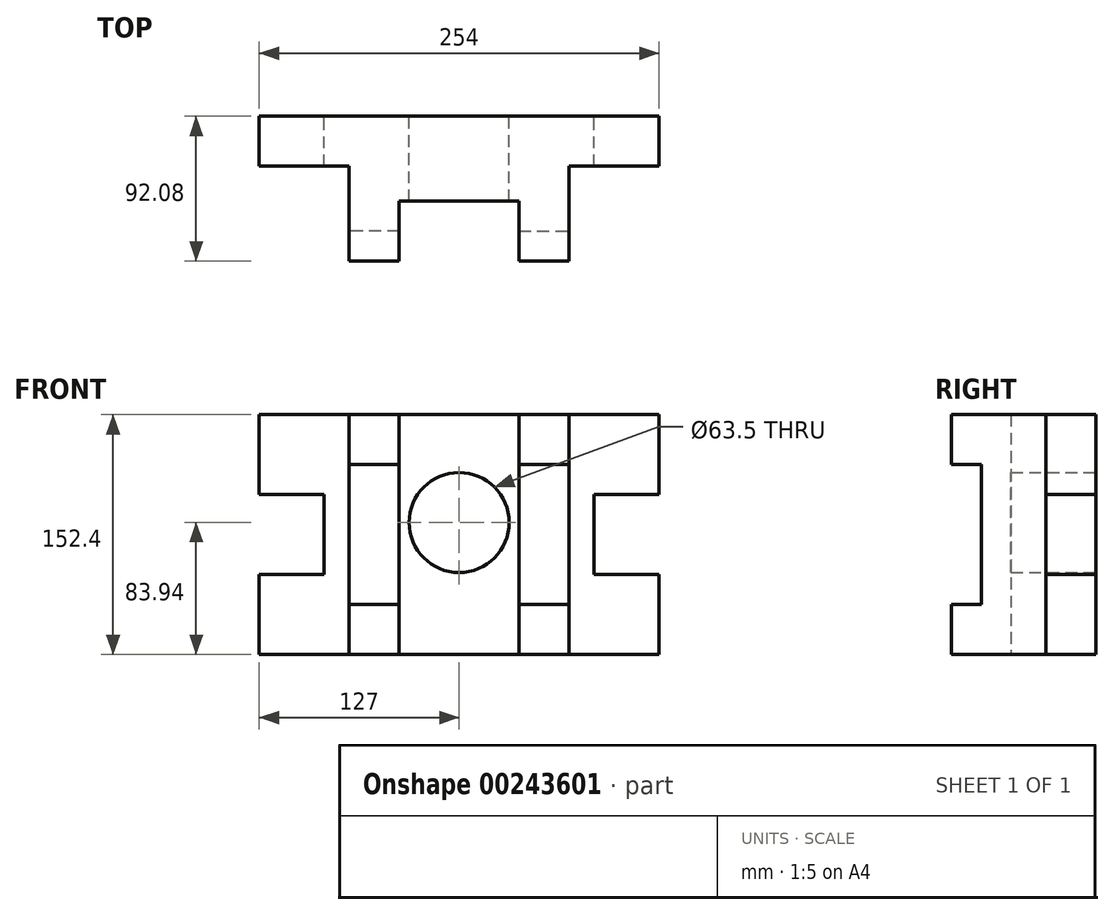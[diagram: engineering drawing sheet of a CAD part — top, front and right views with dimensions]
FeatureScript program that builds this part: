
annotation { "Feature Type Name" : "Feature", "Feature Type Description" : "" }
export const myFeature = defineFeature(function(context is Context, id is Id, definition is map)
    precondition{}
    {
        {
            var Q0;
            Q0=qCreatedBy(makeId("Front.planeOp"),FACE);
            var sketch = newSketch(context, id + "F0", { "sketchPlane" : qUnion([Q0])});
            skLineSegment(sketch, "E0", {"start": v(0, 68.46) * mm, "end": v(0, -79.2) * mm});
            skLineSegment(sketch, "E1.bottom", {"start": v(0, 68.46) * mm, "end": v(38.1, 68.46) * mm});
            skLineSegment(sketch, "E1.top", {"start": v(0, -83.94) * mm, "end": v(38.1, -83.94) * mm});
            skLineSegment(sketch, "E1.left", {"start": v(0, 68.46) * mm, "end": v(0, -83.94) * mm});
            skLineSegment(sketch, "E1.right", {"start": v(38.1, 68.46) * mm, "end": v(38.1, -83.94) * mm});
            skLineSegment(sketch, "E2.bottom", {"start": v(38.1, 68.46) * mm, "end": v(69.85, 68.46) * mm});
            skLineSegment(sketch, "E2.top", {"start": v(38.1, 36.71) * mm, "end": v(69.85, 36.71) * mm});
            skLineSegment(sketch, "E2.left", {"start": v(38.1, 68.46) * mm, "end": v(38.1, 36.71) * mm});
            skLineSegment(sketch, "E2.right", {"start": v(69.85, 68.46) * mm, "end": v(69.85, 36.71) * mm});
            skLineSegment(sketch, "E3.bottom", {"start": v(38.1, -83.94) * mm, "end": v(69.85, -83.94) * mm});
            skLineSegment(sketch, "E3.top", {"start": v(38.1, -52.19) * mm, "end": v(69.85, -52.19) * mm});
            skLineSegment(sketch, "E3.left", {"start": v(38.1, -83.94) * mm, "end": v(38.1, -52.19) * mm});
            skLineSegment(sketch, "E3.right", {"start": v(69.85, -83.94) * mm, "end": v(69.85, -52.19) * mm});
            skLineSegment(sketch, "E4.left", {"start": v(38.1, 36.71) * mm, "end": v(38.1, -52.19) * mm});
            skLineSegment(sketch, "E4.right", {"start": v(69.85, 36.71) * mm, "end": v(69.85, -52.19) * mm});
            skLineSegment(sketch, "E5.bottom", {"start": v(69.85, 68.46) * mm, "end": v(127, 68.46) * mm});
            skLineSegment(sketch, "E5.top", {"start": v(69.85, -83.94) * mm, "end": v(127, -83.94) * mm});
            skLineSegment(sketch, "E5.left", {"start": v(69.85, 68.46) * mm, "end": v(69.85, -83.94) * mm});
            skLineSegment(sketch, "E5.right", {"start": v(127, 68.46) * mm, "end": v(127, 17.66) * mm});
            skLineSegment(sketch, "E6.bottom", {"start": v(127, -83.94) * mm, "end": v(111.13, -83.94) * mm});
            skLineSegment(sketch, "E6.top", {"start": v(127, -33.14) * mm, "end": v(85.72, -33.14) * mm});
            skLineSegment(sketch, "E6.left", {"start": v(127, -83.94) * mm, "end": v(127, -33.14) * mm});
            skLineSegment(sketch, "E7.bottom", {"start": v(85.72, -33.14) * mm, "end": v(127, -33.14) * mm});
            skLineSegment(sketch, "E7.top", {"start": v(85.72, 17.66) * mm, "end": v(127, 17.66) * mm});
            skLineSegment(sketch, "E7.left", {"start": v(85.72, -33.14) * mm, "end": v(85.72, 17.66) * mm});
            skLineSegment(sketch, "E8.MirrorCS", {"start": v(0, 68.46) * mm, "end": v(-38.1, 68.46) * mm});
            skLineSegment(sketch, "E9.MirrorCS", {"start": v(-38.1, 68.46) * mm, "end": v(-38.1, 36.71) * mm});
            skLineSegment(sketch, "E10.MirrorCS", {"start": v(-38.1, 68.46) * mm, "end": v(-38.1, -83.94) * mm});
            skLineSegment(sketch, "E11.MirrorCS", {"start": v(-38.1, 36.71) * mm, "end": v(-69.85, 36.71) * mm});
            skLineSegment(sketch, "E12.MirrorCS", {"start": v(-38.1, -52.19) * mm, "end": v(-69.85, -52.19) * mm});
            skLineSegment(sketch, "E13.MirrorCS", {"start": v(0, -83.94) * mm, "end": v(-38.1, -83.94) * mm});
            skLineSegment(sketch, "E14.MirrorCS", {"start": v(-38.1, -83.94) * mm, "end": v(-69.85, -83.94) * mm});
            skLineSegment(sketch, "E15.MirrorCS", {"start": v(-69.85, -83.94) * mm, "end": v(-127, -83.94) * mm});
            skLineSegment(sketch, "E16.MirrorCS", {"start": v(-127, -33.14) * mm, "end": v(-85.72, -33.14) * mm});
            skLineSegment(sketch, "E17.MirrorCS", {"start": v(-85.72, -33.14) * mm, "end": v(-85.72, 17.66) * mm});
            skLineSegment(sketch, "E18.MirrorCS", {"start": v(-85.72, 17.66) * mm, "end": v(-127, 17.66) * mm});
            skLineSegment(sketch, "E19.MirrorCS", {"start": v(-127, 68.46) * mm, "end": v(-127, 17.66) * mm});
            skLineSegment(sketch, "E20.MirrorCS", {"start": v(-69.85, 68.46) * mm, "end": v(-127, 68.46) * mm});
            skLineSegment(sketch, "E21.MirrorCS", {"start": v(-38.1, 68.46) * mm, "end": v(-69.85, 68.46) * mm});
            skLineSegment(sketch, "E22.MirrorCS", {"start": v(-69.85, -83.94) * mm, "end": v(-69.85, -52.19) * mm});
            skLineSegment(sketch, "E23.MirrorCS", {"start": v(-38.1, -83.94) * mm, "end": v(-38.1, -52.19) * mm});
            skLineSegment(sketch, "E24.MirrorCS", {"start": v(-69.85, 36.71) * mm, "end": v(-69.85, -52.19) * mm});
            skLineSegment(sketch, "E25.MirrorCS", {"start": v(-69.85, 68.46) * mm, "end": v(-69.85, 36.71) * mm});
            skLineSegment(sketch, "E26.MirrorCS", {"start": v(-127, -83.94) * mm, "end": v(-127, -33.14) * mm});
            skArc(sketch, "E27", {"start": v(0, 31.75) * mm, "mid": v(31.75, 0) * mm, "end": v(0, -31.75) * mm});
            skArc(sketch, "E28.MirrorCS", {"start": v(0, 31.75) * mm, "mid": v(-31.75, 0) * mm, "end": v(0, -31.75) * mm});
            skSolve(sketch);
        }
        {
            var Q0;
            Q0=makeQuery(id+"F0.imprint","IMPRINT",FACE,{"disambiguationData":[TD([[makeQuery(id+"F0.imprint","IMPRINT",EDGE,{"derivedFrom":sQuery(id+"F0.wireOp",EDGE,"E11.MirrorCS")}),-1.0]])]});
            extrude(context, id + "F1", {"entities" : qUnion([Q0]), "depth" : 92.07 * mm});
        }
        {
            var Q0;
            {var subQ0=sQuery(id+"F0.wireOp",EDGE,"E14.MirrorCS");Q0=makeQuery(id+"F0.imprint","IMPRINT",FACE,{"disambiguationData":[TD([[makeQuery(id+"F0.imprint","IMPRINT",EDGE,{"derivedFrom":subQ0}),-1.0]])]});}
            extrude(context, id + "F2", {"entities" : qUnion([Q0]), "depth" : 92.07 * mm});
        }
        {
            var Q0;
            {var subQ0=sQuery(id+"F0.wireOp",EDGE,"E3.bottom");Q0=makeQuery(id+"F0.imprint","IMPRINT",FACE,{"disambiguationData":[TD([[makeQuery(id+"F0.imprint","IMPRINT",EDGE,{"derivedFrom":subQ0}),1.0]])]});}
            extrude(context, id + "F3", {"entities" : qUnion([Q0]), "depth" : 92.07 * mm});
        }
        {
            var Q0;
            {var subQ0=sQuery(id+"F0.wireOp",EDGE,"E2.bottom");Q0=makeQuery(id+"F0.imprint","IMPRINT",FACE,{"disambiguationData":[TD([[makeQuery(id+"F0.imprint","IMPRINT",EDGE,{"derivedFrom":subQ0}),-1.0]])]});}
            extrude(context, id + "F4", {"entities" : qUnion([Q0]), "depth" : 92.07 * mm});
        }
        {
            var Q0;
            {var subQ1=sQuery(id+"F0.wireOp",EDGE,"E5.bottom");Q0=makeQuery(id+"F0.imprint","IMPRINT",FACE,{"disambiguationData":[TD([[makeQuery(id+"F0.imprint","IMPRINT",EDGE,{"derivedFrom":subQ1}),-1.0]])]});}
            extrude(context, id + "F5", {"entities" : qUnion([Q0]), "operationType" : NewBodyOperationType.ADD, "depth" : 31.75 * mm});
        }
        {
            var Q0;
            Q0=makeQuery(id+"F0.imprint","IMPRINT",FACE,{"disambiguationData":[TD([[makeQuery(id+"F0.imprint","IMPRINT",EDGE,{"derivedFrom":sQuery(id+"F0.wireOp",EDGE,"E15.MirrorCS")}),-1.0]])]});
            extrude(context, id + "F6", {"entities" : qUnion([Q0]), "operationType" : NewBodyOperationType.ADD, "depth" : 31.75 * mm});
        }
        {
            var Q0;
            {var subQ0=sQuery(id+"F0.wireOp",EDGE,"E12.MirrorCS");Q0=makeQuery(id+"F0.imprint","IMPRINT",FACE,{"disambiguationData":[TD([[makeQuery(id+"F0.imprint","IMPRINT",EDGE,{"derivedFrom":subQ0}),-1.0]])]});}
            extrude(context, id + "F7", {"entities" : qUnion([Q0]), "depth" : 73.02 * mm});
        }
        {
            var Q0;
            {var subQ0=sQuery(id+"F0.wireOp",EDGE,"E2.top");Q0=makeQuery(id+"F0.imprint","IMPRINT",FACE,{"disambiguationData":[TD([[makeQuery(id+"F0.imprint","IMPRINT",EDGE,{"derivedFrom":subQ0}),-1.0]])]});}
            extrude(context, id + "F8", {"entities" : qUnion([Q0]), "depth" : 73.02 * mm});
        }
        {
            var Q0;
            {var subQ0=sQuery(id+"F0.wireOp",EDGE,"E8.MirrorCS");Q0=makeQuery(id+"F0.imprint","IMPRINT",FACE,{"disambiguationData":[TD([[makeQuery(id+"F0.imprint","IMPRINT",EDGE,{"derivedFrom":subQ0}),1.0]])]});}
            extrude(context, id + "F9", {"entities" : qUnion([Q0]), "operationType" : NewBodyOperationType.ADD, "depth" : 53.97 * mm});
        }
        {
            var Q0;
            {var subQ4=sQuery(id+"F0.wireOp",EDGE,"E1.bottom");Q0=makeQuery(id+"F0.imprint","IMPRINT",FACE,{"disambiguationData":[TD([[makeQuery(id+"F0.imprint","IMPRINT",EDGE,{"derivedFrom":subQ4}),-1.0]])]});}
            extrude(context, id + "F10", {"entities" : qUnion([Q0]), "operationType" : NewBodyOperationType.ADD, "depth" : 53.97 * mm});
        }
    });
